# Revit family: FU_Inspec_Grade_3-1
name_source: partatom
category: Furniture
units: mm (PartAtom-declared; Revit-internal decimal feet)

## family parameters
Always vertical = Yes
Cut with Voids When Loaded = No
OmniClass Number = 23.40.20.00
OmniClass Title = General Furniture and Specialties
Room Calculation Point = No
Shared = No
Work Plane-Based = No

## types (3) — shared parameters
Assembly Code = E2020
Depth = 550 mm
Height = 1120 mm  [stored 3.67454 ft]
Keynote = 46.B
Manufacturer = Inspec
URL = https://inspecfurniture.com
Weight = 6.7
Width = 520 mm  [stored 1.70604 ft]
zero-valued in all types: Default Elevation

## per-type parameters (varying)
| type | Description | Frame Material | Model | Seat Material | Seat Pad Material |
| Grade 3.1 - Red - Red | Barstool with recycled polypropylene seat and back on on powder coated or chromium plated steel tubular frame and footrest | Colour - Coated - Dark red | Grade 3.1 | Colour - Coated - Dark red | Fabric - Divina Red |
| Grade 3.2 - Black - Red | Barstool with recycled polypropylene seat and back on on powder coated or chromium plated steel tubular frame and footrest. Seat upholstered | Colour - Coated - Black | Grade 3.2 | Colour - Coated - Dark red | Fabric - Divina Beige |
| Grade 3.3 - Black - Blue | Barstool with fully upholstered recycled polypropylene seat and back on on powder coated or chromium plated steel tubular frame and footrest. | Colour - Coated - Black | Grade 3.3 | Fabric - Divina Blue | Fabric - Divina Beige |

note: [stored X ft] marks values corroborated as IEEE doubles in the binary element streams (Revit-internal decimal feet)

## geometry (parser evidence)
native form markers: Blend x458, Sweep x2
no freeform markers — native parametric forms only
